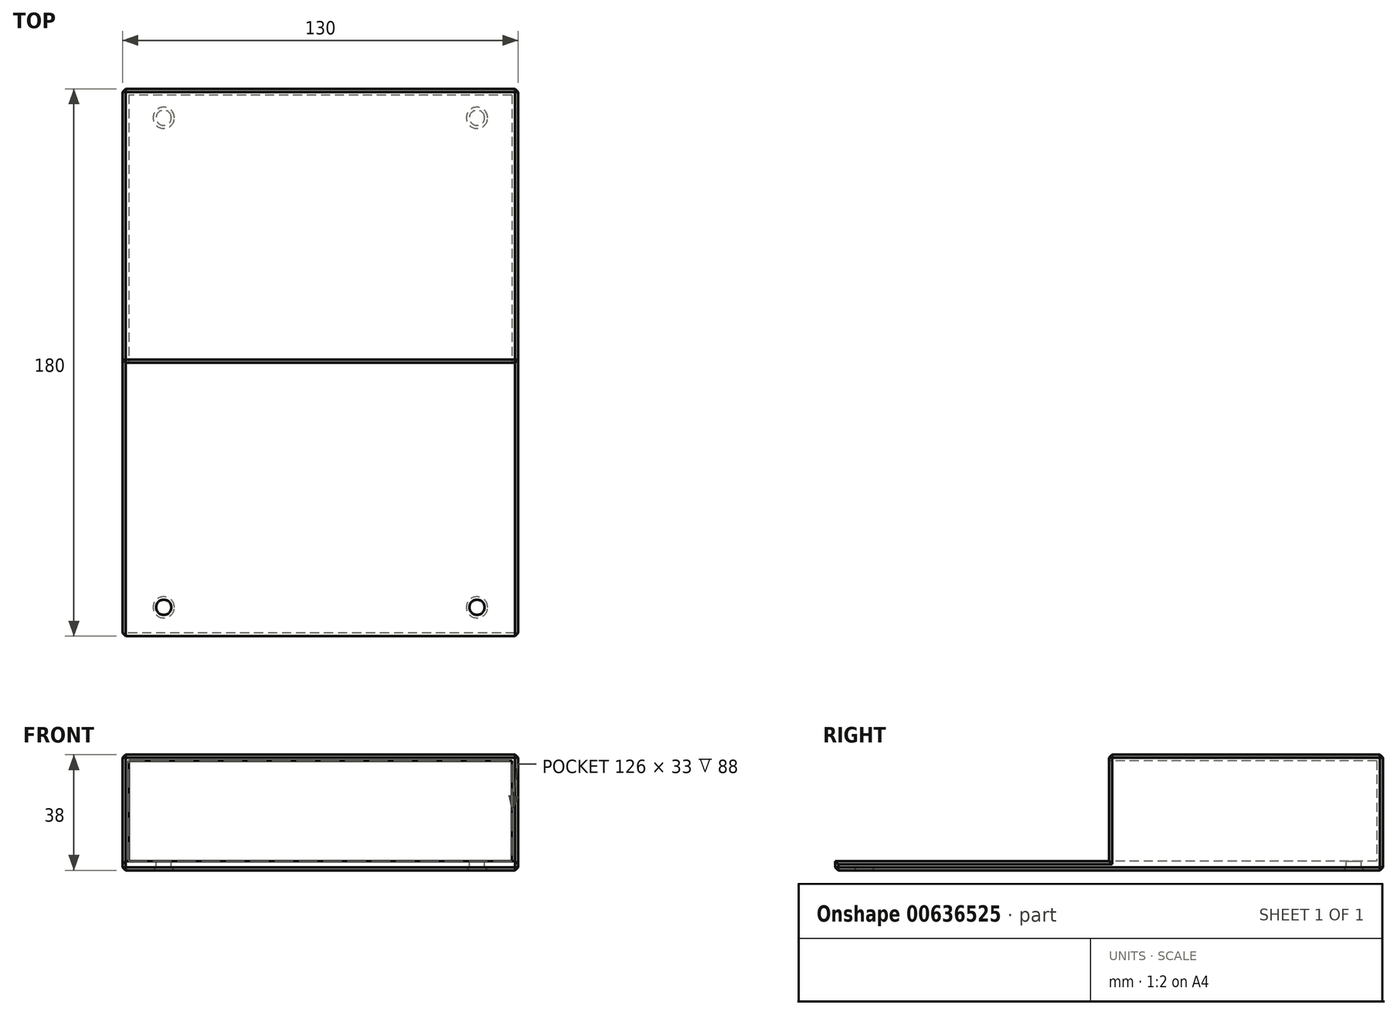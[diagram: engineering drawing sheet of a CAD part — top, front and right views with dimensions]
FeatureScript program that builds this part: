
annotation { "Feature Type Name" : "Feature", "Feature Type Description" : "" }
export const myFeature = defineFeature(function(context is Context, id is Id, definition is map)
    precondition{}
    {
        {
            var Q0;
            Q0=qCreatedBy(makeId("Top.planeOp"),FACE);
            var sketch = newSketch(context, id + "F0", { "sketchPlane" : qUnion([Q0])});
            skLineSegment(sketch, "E0.bottom", {"start": v(51.5, 80.5) * mm, "end": v(-51.5, 80.5) * mm, "construction": true});
            skLineSegment(sketch, "E0.top", {"start": v(51.5, -80.5) * mm, "end": v(-51.5, -80.5) * mm, "construction": true});
            skLineSegment(sketch, "E0.left", {"start": v(51.5, 80.5) * mm, "end": v(51.5, -80.5) * mm, "construction": true});
            skLineSegment(sketch, "E0.right", {"start": v(-51.5, 80.5) * mm, "end": v(-51.5, -80.5) * mm, "construction": true});
            skPoint(sketch, "E0.middle", {"position": v(0, 0) * mm});
            skLineSegment(sketch, "E1.bottom", {"start": v(65, 90) * mm, "end": v(-65, 90) * mm});
            skLineSegment(sketch, "E1.top", {"start": v(65, -90) * mm, "end": v(-65, -90) * mm});
            skLineSegment(sketch, "E1.left", {"start": v(65, 90) * mm, "end": v(65, -90) * mm});
            skLineSegment(sketch, "E1.right", {"start": v(-65, 90) * mm, "end": v(-65, -90) * mm});
            skCircle(sketch, "E2", {"center": v(-51.5, 80.5) * mm, "radius": 2.5 * mm});
            skCircle(sketch, "E3", {"center": v(51.5, 80.5) * mm, "radius": 2.5 * mm});
            skCircle(sketch, "E4", {"center": v(51.5, -80.5) * mm, "radius": 2.5 * mm});
            skCircle(sketch, "E5", {"center": v(-51.5, -80.5) * mm, "radius": 2.5 * mm});
            skLineSegment(sketch, "E6", {"start": v(-65, 0) * mm, "end": v(65, 0) * mm, "construction": true});
            skLineSegment(sketch, "E7.0", {"start": v(-63, 88) * mm, "end": v(-63, -88) * mm});
            skLineSegment(sketch, "E7.1", {"start": v(63, 88) * mm, "end": v(-63, 88) * mm});
            skLineSegment(sketch, "E7.2", {"start": v(63, 88) * mm, "end": v(63, -88) * mm});
            skLineSegment(sketch, "E7.3", {"start": v(63, -88) * mm, "end": v(-63, -88) * mm});
            skLineSegment(sketch, "E8", {"start": v(-65, 0) * mm, "end": v(-63, 0) * mm});
            skLineSegment(sketch, "E9", {"start": v(65, 0) * mm, "end": v(63, 0) * mm});
            skLineSegment(sketch, "E10", {"start": v(-63, 0) * mm, "end": v(63, 0) * mm});
            skSolve(sketch);
        }
        {
            var Q0;
            Q0=makeQuery(id+"F0.imprint","IMPRINT",FACE,{"disambiguationData":[TD([[makeQuery(id+"F0.imprint","IMPRINT",EDGE,{"derivedFrom":sQuery(id+"F0.wireOp",EDGE,"E2")}),-1.0]])]});
            var Q1;
            {var subQ1=sQuery(id+"F0.wireOp",EDGE,"E1.top");Q1=makeQuery(id+"F0.imprint","IMPRINT",FACE,{"disambiguationData":[TD([[makeQuery(id+"F0.imprint","IMPRINT",EDGE,{"derivedFrom":subQ1}),-1.0]])]});}
            var Q2;
            {var subQ1=sQuery(id+"F0.wireOp",EDGE,"E1.bottom");Q2=makeQuery(id+"F0.imprint","IMPRINT",FACE,{"disambiguationData":[TD([[makeQuery(id+"F0.imprint","IMPRINT",EDGE,{"derivedFrom":subQ1}),1.0]])]});}
            var Q3;
            Q3=makeQuery(id+"F0.imprint","IMPRINT",FACE,{"disambiguationData":[TD([[makeQuery(id+"F0.imprint","IMPRINT",EDGE,{"derivedFrom":sQuery(id+"F0.wireOp",EDGE,"E4")}),-1.0]])]});
            extrude(context, id + "F1", {"entities" : qUnion([Q0, Q1, Q2, Q3]), "oppositeDirection" : true, "depth" : 3 * mm, "offsetDistance" : 25 * mm});
        }
        {
            var Q0;
            {var subQ1=sQuery(id+"F0.wireOp",EDGE,"E1.bottom");Q0=makeQuery(id+"F0.imprint","IMPRINT",FACE,{"disambiguationData":[TD([[makeQuery(id+"F0.imprint","IMPRINT",EDGE,{"derivedFrom":subQ1}),1.0]])]});}
            extrude(context, id + "F2", {"entities" : qUnion([Q0]), "operationType" : NewBodyOperationType.ADD, "depth" : 35 * mm, "offsetDistance" : 25 * mm});
        }
        {
            var Q0;
            Q0=makeQuery(id+"F0.imprint","IMPRINT",FACE,{"disambiguationData":[TD([[makeQuery(id+"F0.imprint","IMPRINT",EDGE,{"derivedFrom":sQuery(id+"F0.wireOp",EDGE,"E2")}),-1.0]])]});
            var Q1;
            {var subQ1=sQuery(id+"F0.wireOp",EDGE,"E1.bottom");Q1=makeQuery(id+"F0.imprint","IMPRINT",FACE,{"disambiguationData":[TD([[makeQuery(id+"F0.imprint","IMPRINT",EDGE,{"derivedFrom":subQ1}),1.0]])]});}
            var Q2;
            Q2=makeQuery(id+"F0.imprint","IMPRINT",FACE,{"disambiguationData":[TD([[makeQuery(id+"F0.imprint","IMPRINT",EDGE,{"derivedFrom":sQuery(id+"F0.wireOp",EDGE,"E2")}),1.0]])]});
            var Q3;
            Q3=makeQuery(id+"F0.imprint","IMPRINT",FACE,{"disambiguationData":[TD([[makeQuery(id+"F0.imprint","IMPRINT",EDGE,{"derivedFrom":sQuery(id+"F0.wireOp",EDGE,"E3")}),1.0]])]});
            extrude(context, id + "F3", {"entities" : qUnion([Q0, Q1, Q2, Q3]), "operationType" : NewBodyOperationType.ADD, "depth" : 35 * mm, "offsetDistance" : 25 * mm, "hasSecondDirection" : true, "secondDirectionOppositeDirection" : false, "secondDirectionDepth" : 33 * mm});
        }
        {
            var Q0;
            {var subQ0=sQuery(id+"F0.wireOp",EDGE,"E9");var subQ1=sQuery(id+"F0.wireOp",EDGE,"E8");var subQ2=sQuery(id+"F0.wireOp",EDGE,"E1.right");var subQ3=sQuery(id+"F0.wireOp",EDGE,"E1.left");var subQ4=sQuery(id+"F0.wireOp",EDGE,"E1.bottom");Q0=makeQuery(id+"F3.boolean.opBoolean","MERGE",FACE,{"derivedFrom":[makeQuery(id+"F2.opExtrude","CAP_FACE",FACE,{"disambiguationData":[OSD([subQ4,subQ3,subQ2,sQuery(id+"F0.wireOp",EDGE,"E7.0"),sQuery(id+"F0.wireOp",EDGE,"E7.1"),sQuery(id+"F0.wireOp",EDGE,"E7.2"),subQ1,subQ0])],"isStart":false}),makeQuery(id+"F3.opExtrude","CAP_FACE",FACE,{"disambiguationData":[OSD([subQ4,subQ3,subQ2,subQ1,subQ0,sQuery(id+"F0.wireOp",EDGE,"E10")])],"isStart":false})]});}
            var Q1;
            {var subQ0=sQuery(id+"F0.wireOp",EDGE,"E1.right");Q1=makeQuery(id+"F2.boolean.opBoolean","MERGE",FACE,{"derivedFrom":[makeQuery(id+"F1.opExtrude","SWEPT_FACE",FACE,{"disambiguationData":[OSD([subQ0])]}),makeQuery(id+"F2.opExtrude","SWEPT_FACE",FACE,{"disambiguationData":[OSD([subQ0])]})]});}
            var Q2;
            {var subQ0=sQuery(id+"F0.wireOp",EDGE,"E1.bottom");Q2=makeQuery(id+"F2.boolean.opBoolean","MERGE",FACE,{"derivedFrom":[makeQuery(id+"F1.opExtrude","SWEPT_FACE",FACE,{"disambiguationData":[OSD([subQ0])]}),makeQuery(id+"F2.opExtrude","SWEPT_FACE",FACE,{"disambiguationData":[OSD([subQ0])]})]});}
            var Q3;
            {var subQ0=sQuery(id+"F0.wireOp",EDGE,"E1.left");Q3=makeQuery(id+"F2.boolean.opBoolean","MERGE",FACE,{"derivedFrom":[makeQuery(id+"F1.opExtrude","SWEPT_FACE",FACE,{"disambiguationData":[OSD([subQ0])]}),makeQuery(id+"F2.opExtrude","SWEPT_FACE",FACE,{"disambiguationData":[OSD([subQ0])]})]});}
            var Q4;
            Q4=makeQuery(id+"F1.opExtrude","CAP_FACE",FACE,{"disambiguationData":[OSD([sQuery(id+"F0.wireOp",EDGE,"E1.bottom"),sQuery(id+"F0.wireOp",EDGE,"E1.top"),sQuery(id+"F0.wireOp",EDGE,"E1.left"),sQuery(id+"F0.wireOp",EDGE,"E1.right"),sQuery(id+"F0.wireOp",EDGE,"E2"),sQuery(id+"F0.wireOp",EDGE,"E3"),sQuery(id+"F0.wireOp",EDGE,"E4"),sQuery(id+"F0.wireOp",EDGE,"E5")])],"isStart":false});
            chamfer(context, id + "F4", {"entities" : qUnion([Q0, Q1, Q2, Q3, Q4]), "width" : 1 * mm, "tangentPropagation" : true});
        }
    });
